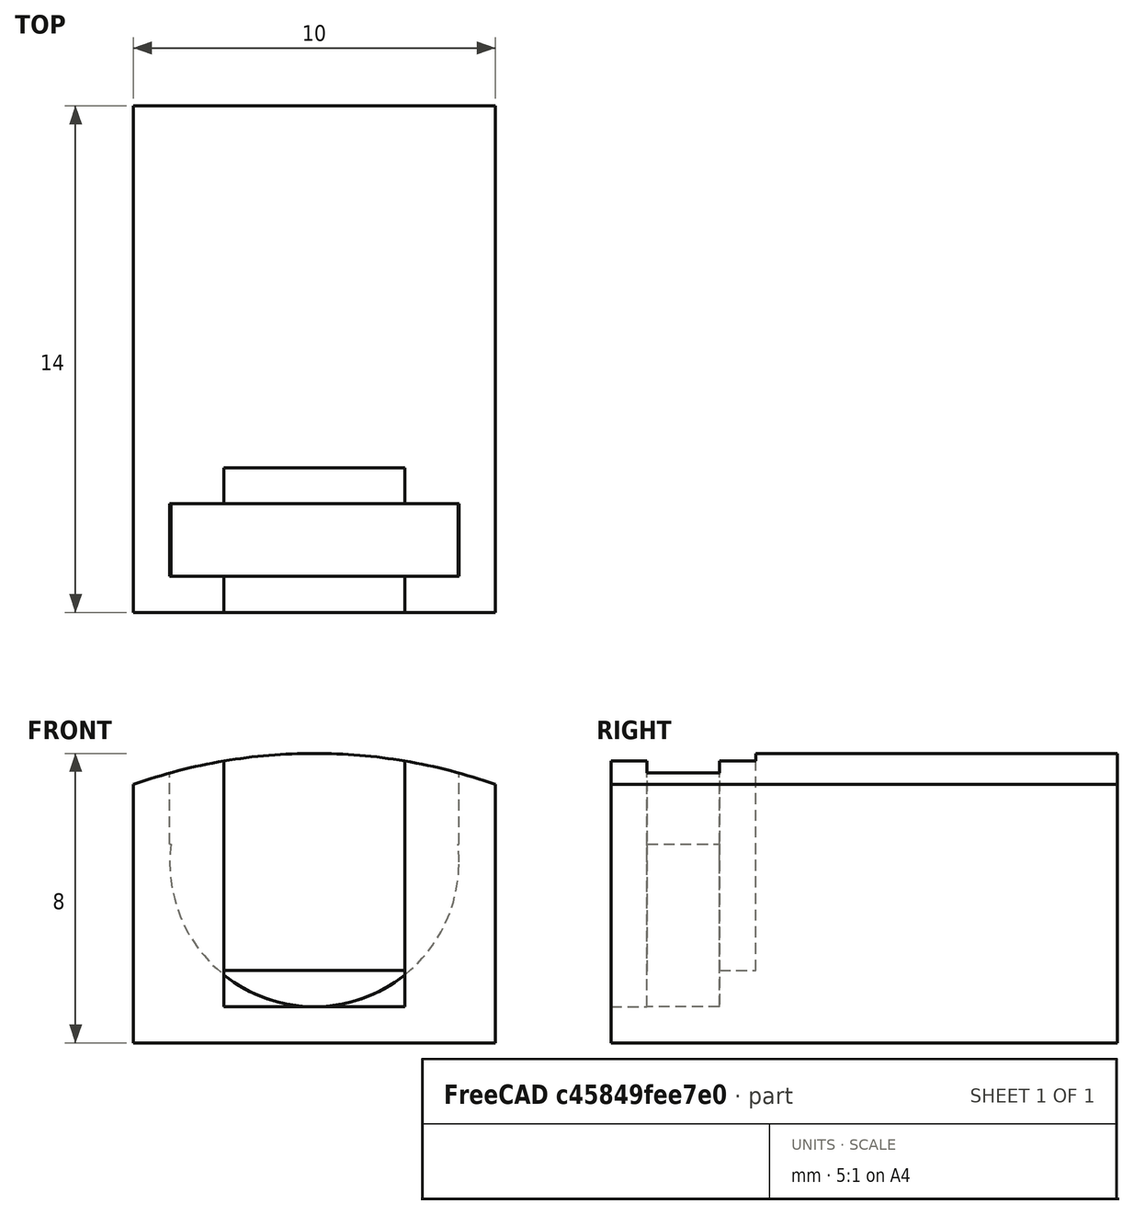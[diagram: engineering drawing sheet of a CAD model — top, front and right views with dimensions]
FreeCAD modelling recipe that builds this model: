
FCSTD DOCUMENT  (FreeCAD 0.16R4924 (Git))
Label: pin_v2.2
License: All rights reserved
LicenseURL: http://en.wikipedia.org/wiki/All_rights_reserved
objects: Part::Box×5, Part::Cut×5, Part::Cylinder×2, Part::MultiCommon×1, Part::Feature×1, App::MeasureDistance×1
note: 14 computed .brp shape members not serialized (recipe doc carries the construction recipe); baked Part::Feature solids carry a one-line shape summary decoded from their .brp

FEATURE [Part::Box] Box  label="pin"
  Height = 8
  Length = 10
  Width = 20
FEATURE [Part::Cylinder] Cylinder  label="solenoid_head_slot"
  Angle = 360
  Height = 2
  Placement = pos=(5,3,5) rot=(1,0,0;1.5708rad)
  Radius = 4
FEATURE [Part::Cut] Cut
  Base = -> Box
  Tool = -> Cylinder
FEATURE [Part::Box] Box001  label="end_opening"
  Height = 7
  Length = 5
  Placement = pos=(2.5,0,1) rot=(0,0,1;0rad)
  Width = 1
FEATURE [Part::Cut] Cut001
  Base = -> Cut
  Tool = -> Box001
FEATURE [Part::Box] Box002  label="interior_opening"
  Height = 6
  Length = 5
  Placement = pos=(2.5,3,2) rot=(0,0,1;0rad)
  Width = 1
FEATURE [Part::Cut] Cut002
  Base = -> Cut001
  Tool = -> Box002
FEATURE [Part::Box] Box003  label="cylinder_edge_refinement"
  Height = 2.5
  Length = 8
  Placement = pos=(1,1,5.5) rot=(0,0,1;0rad)
  Width = 2
FEATURE [Part::Cut] Cut003
  Base = -> Cut002
  Tool = -> Box003
FEATURE [Part::Cylinder] Cylinder001  label="rounded_top"
  Angle = 360
  Height = 30
  Placement = pos=(5,25,-7) rot=(1,0,0;1.5708rad)
  Radius = 15
FEATURE [Part::MultiCommon] Common
  Shapes = -> [Cut003,Cylinder001]
FEATURE [Part::Feature] Common_cs  label="pin_cs"
  shape: bbox 10 x 2e-07 x 8 mm, 0 faces, 0 solids (baked)
FEATURE [Part::Box] Box004  label="end_offcut"
  Height = 10
  Length = 10
  Placement = pos=(0,14,0) rot=(0,0,1;0rad)
  Width = 10
FEATURE [Part::Cut] Cut004
  Base = -> Common
  Tool = -> Box004
FEATURE [App::MeasureDistance] Distance  label="Distance: 8.000"
  Distance = 8.00013
  P1 = (9,1.99182,7.45683)
  P2 = (1,1.94558,7.45683)
